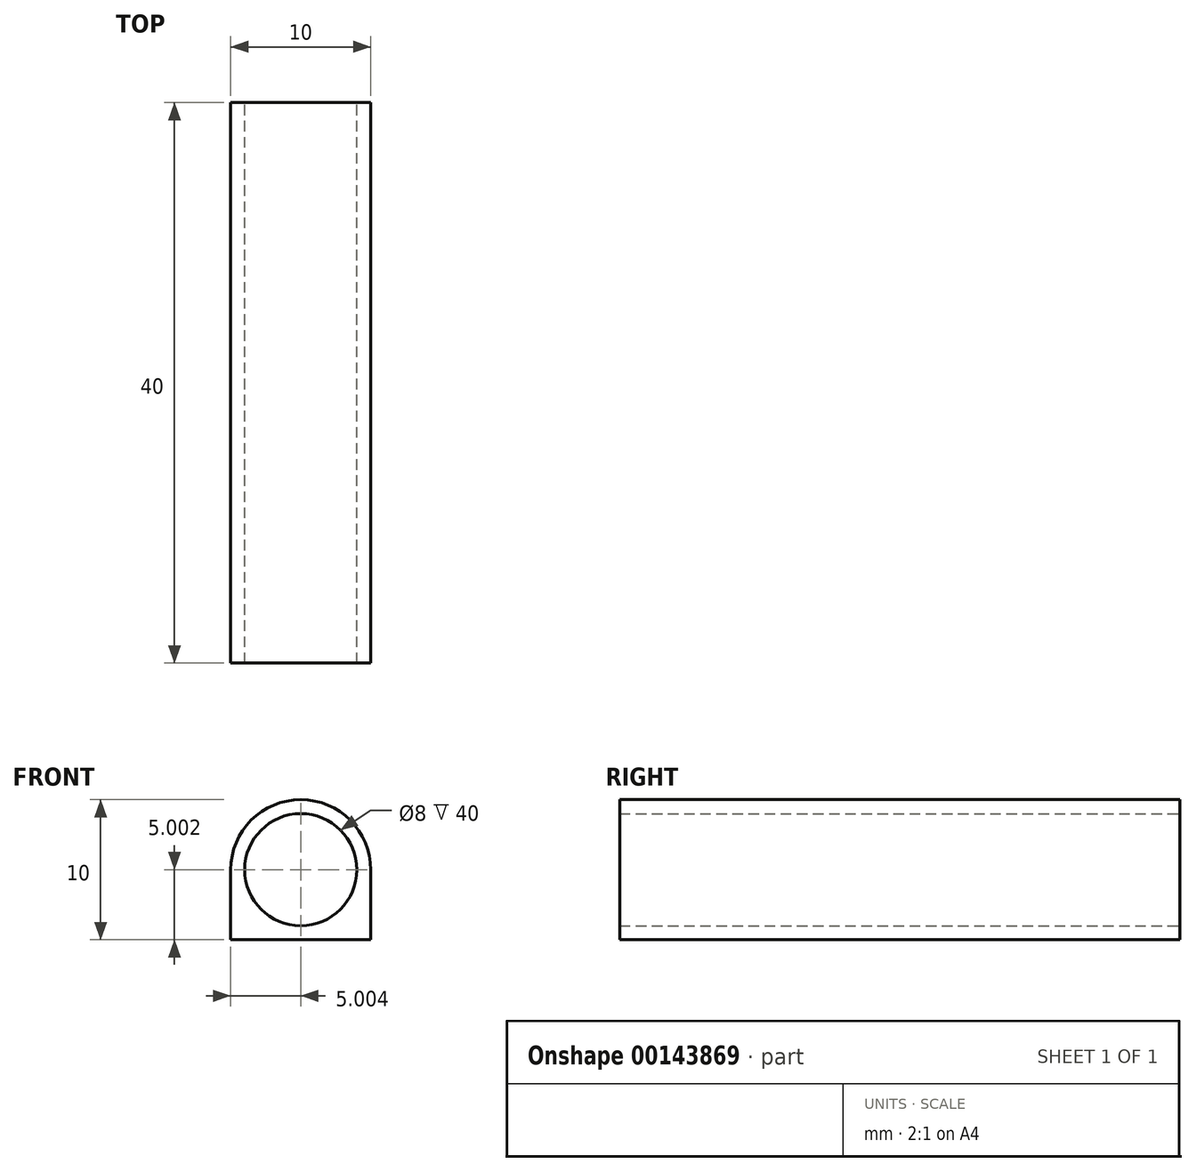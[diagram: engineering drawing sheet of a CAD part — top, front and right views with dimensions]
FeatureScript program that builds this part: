
annotation { "Feature Type Name" : "Feature", "Feature Type Description" : "" }
export const myFeature = defineFeature(function(context is Context, id is Id, definition is map)
    precondition{}
    {
        {
            var Q0;
            Q0=qCreatedBy(makeId("Front.planeOp"),FACE);
            var sketch = newSketch(context, id + "F0", { "sketchPlane" : qUnion([Q0])});
            skCircle(sketch, "E0", {"center": v(-5.39, 21.18) * mm, "radius": 4 * mm});
            skCircle(sketch, "E1", {"center": v(-5.39, 21.18) * mm, "radius": 5 * mm});
            skLineSegment(sketch, "E2", {"start": v(-10.39, 21.18) * mm, "end": v(-10.39, 16.18) * mm});
            skLineSegment(sketch, "E3", {"start": v(-10.39, 16.18) * mm, "end": v(-0.39, 16.18) * mm});
            skLineSegment(sketch, "E4", {"start": v(-0.39, 21.18) * mm, "end": v(-0.39, 16.18) * mm});
            skSolve(sketch);
        }
        {
            var Q0;
            {var subQ0=sQuery(id+"F0.wireOp",EDGE,"E2");Q0=makeQuery(id+"F0.imprint","IMPRINT",FACE,{"disambiguationData":[TD([[makeQuery(id+"F0.imprint","IMPRINT",EDGE,{"derivedFrom":subQ0}),1.0]])]});}
            var Q1;
            Q1=makeQuery(id+"F0.imprint","IMPRINT",FACE,{"disambiguationData":[TD([[makeQuery(id+"F0.imprint","IMPRINT",EDGE,{"derivedFrom":sQuery(id+"F0.wireOp",EDGE,"E0")}),-1.0]])]});
            var Q2;
            {var subQ0=sQuery(id+"F0.wireOp",EDGE,"E4");Q2=makeQuery(id+"F0.imprint","IMPRINT",FACE,{"disambiguationData":[TD([[makeQuery(id+"F0.imprint","IMPRINT",EDGE,{"derivedFrom":subQ0}),-1.0]])]});}
            extrude(context, id + "F1", {"entities" : qUnion([Q0, Q1, Q2]), "depth" : 40 * mm, "offsetDistance" : 25 * mm});
        }
    });
